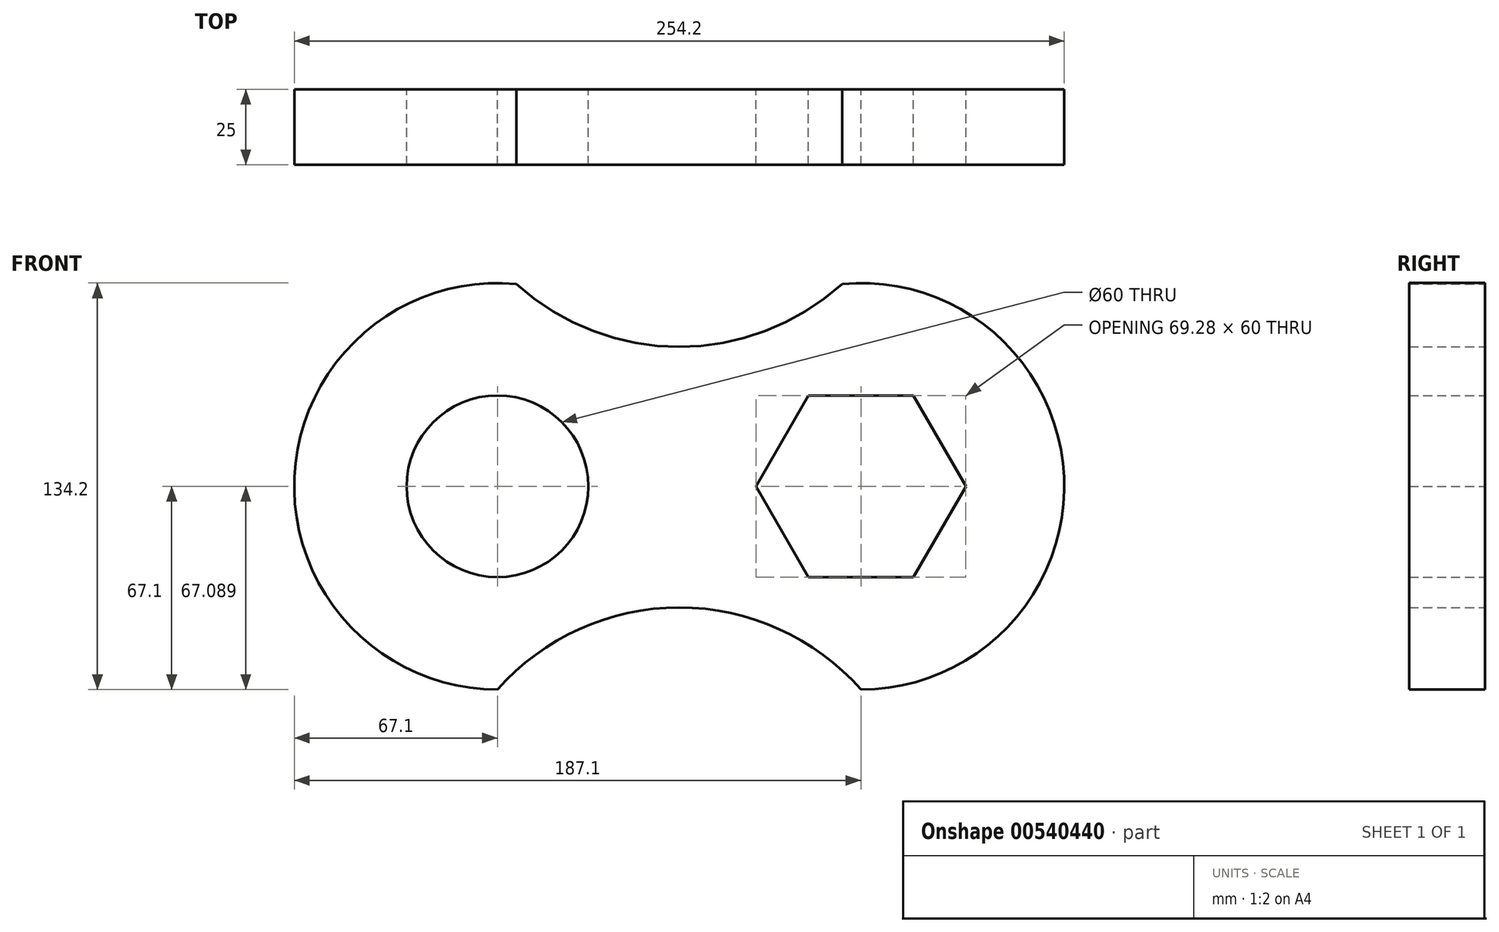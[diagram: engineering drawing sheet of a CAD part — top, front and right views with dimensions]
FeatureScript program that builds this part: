
annotation { "Feature Type Name" : "Feature", "Feature Type Description" : "" }
export const myFeature = defineFeature(function(context is Context, id is Id, definition is map)
    precondition{}
    {
        {
            var Q0;
            Q0=qCreatedBy(makeId("Front.planeOp"),FACE);
            var sketch = newSketch(context, id + "F0", { "sketchPlane" : qUnion([Q0])});
            skCircle(sketch, "E0", {"center": v(0, 0) * mm, "radius": 30 * mm});
            skPoint(sketch, "E1.0.midPoint", {"position": v(88.41, -18.24) * mm});
            skArc(sketch, "E2", {"start": v(6.2, 66.82) * mm, "mid": v(-67.03, 3.1) * mm, "end": v(0, -67.1) * mm});
            skPoint(sketch, "E3.orphan", {"position": v(77.89, 0) * mm});
            skPoint(sketch, "E1.0.start.orphan", {"position": v(98.94, -36.47) * mm});
            skPoint(sketch, "E4.0.midPoint", {"position": v(145.98, -17.28) * mm});
            skPoint(sketch, "E5.orphan", {"position": v(137.34, -32.24) * mm});
            skPoint(sketch, "E4.5.end.orphan", {"position": v(154.62, -2.32) * mm});
            skCircle(sketch, "E6.cCircle", {"center": v(120, -0.01) * mm, "radius": 30 * mm, "construction": true});
            skLineSegment(sketch, "E6.0", {"start": v(154.64, -0.01) * mm, "end": v(137.32, -30.01) * mm});
            skLineSegment(sketch, "E6.1", {"start": v(137.32, -30.01) * mm, "end": v(102.68, -30.01) * mm});
            skLineSegment(sketch, "E6.2", {"start": v(102.68, -30.01) * mm, "end": v(85.36, -0.01) * mm});
            skLineSegment(sketch, "E6.3", {"start": v(85.36, -0.01) * mm, "end": v(102.68, 29.99) * mm});
            skLineSegment(sketch, "E6.4", {"start": v(102.68, 29.99) * mm, "end": v(137.32, 29.99) * mm});
            skLineSegment(sketch, "E6.5", {"start": v(137.32, 29.99) * mm, "end": v(154.64, -0.01) * mm});
            skPoint(sketch, "E6.0.midPoint", {"position": v(145.98, -15.01) * mm});
            skLineSegment(sketch, "E7.trimOffspring", {"start": v(85.36, 0) * mm, "end": v(90, 0) * mm});
            skArc(sketch, "E8.MirrorCS", {"start": v(113.8, 66.82) * mm, "mid": v(187.03, 3.1) * mm, "end": v(120, -67.1) * mm});
            skArc(sketch, "E9", {"start": v(6.2, 66.82) * mm, "mid": v(60, 46.02) * mm, "end": v(113.8, 66.82) * mm});
            skArc(sketch, "E10", {"start": v(120, -67.1) * mm, "mid": v(60, -40.02) * mm, "end": v(0, -67.1) * mm});
            skSolve(sketch);
        }
        {
            var Q0;
            Q0=makeQuery(id+"F0.imprint","IMPRINT",FACE,{"disambiguationData":[TD([[makeQuery(id+"F0.imprint","IMPRINT",EDGE,{"derivedFrom":sQuery(id+"F0.wireOp",EDGE,"E0")}),-1.0]])]});
            extrude(context, id + "F1", {"entities" : qUnion([Q0]), "depth" : 25 * mm, "offsetDistance" : 25 * mm});
        }
    });
